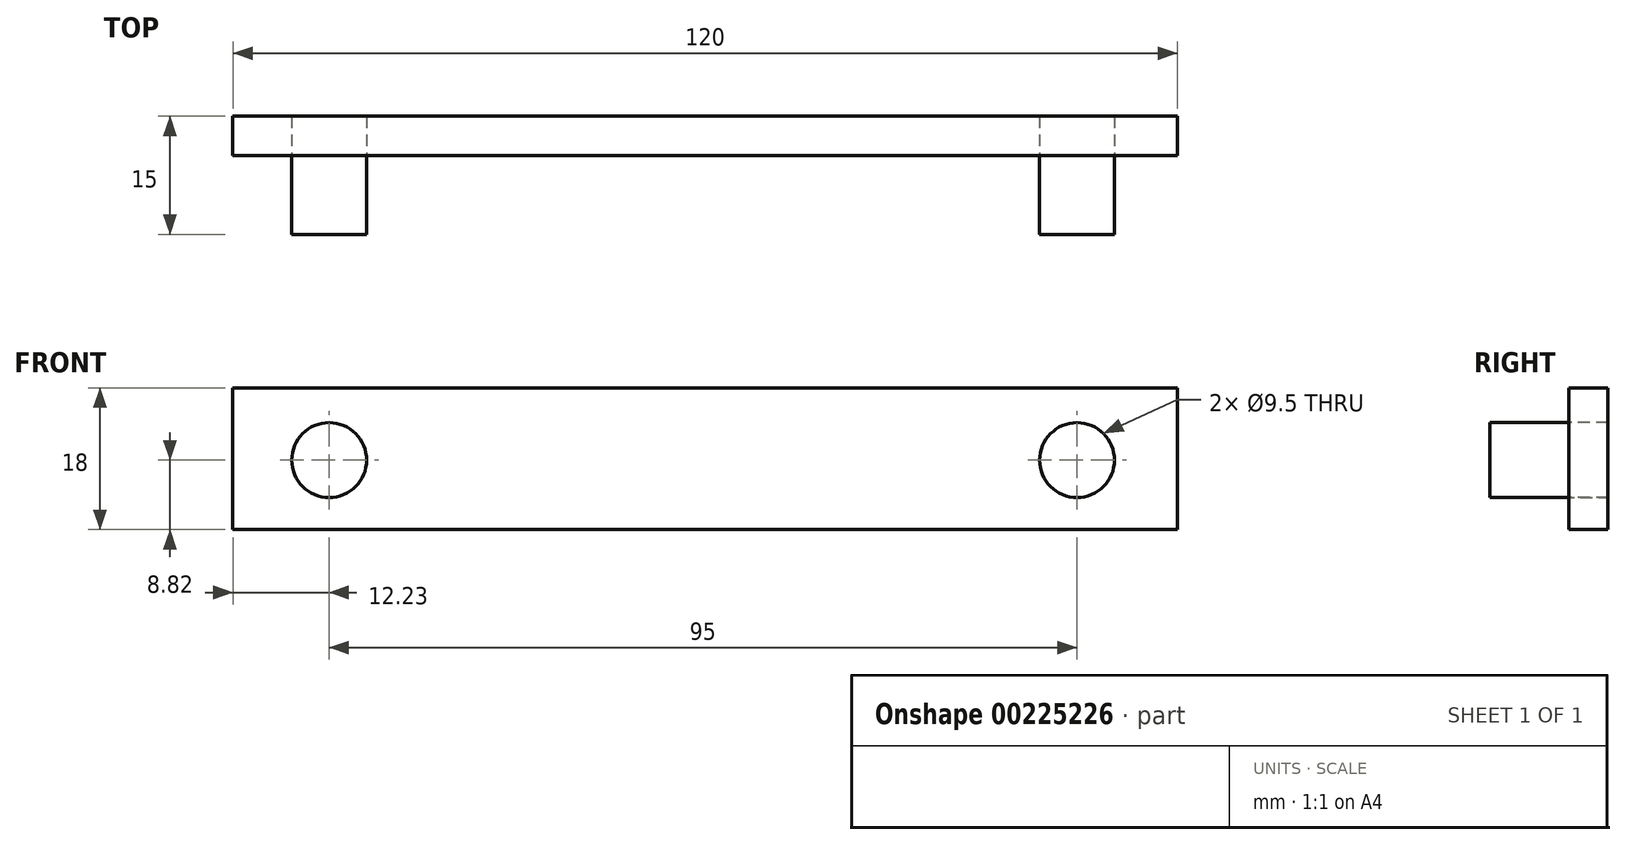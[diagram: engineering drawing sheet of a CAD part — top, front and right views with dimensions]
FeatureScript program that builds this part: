
annotation { "Feature Type Name" : "Feature", "Feature Type Description" : "" }
export const myFeature = defineFeature(function(context is Context, id is Id, definition is map)
    precondition{}
    {
        {
            var Q0;
            Q0=qCreatedBy(makeId("Front.planeOp"),FACE);
            var sketch = newSketch(context, id + "F0", { "sketchPlane" : qUnion([Q0])});
            skCircle(sketch, "E0", {"center": v(0, 0) * mm, "radius": 4.75 * mm});
            skLineSegment(sketch, "E1.bottom", {"start": v(-12.23, 9.18) * mm, "end": v(107.77, 9.18) * mm});
            skLineSegment(sketch, "E1.top", {"start": v(-12.23, -8.82) * mm, "end": v(107.77, -8.82) * mm});
            skLineSegment(sketch, "E1.left", {"start": v(-12.23, 9.18) * mm, "end": v(-12.23, -8.82) * mm});
            skLineSegment(sketch, "E1.right", {"start": v(107.77, 9.18) * mm, "end": v(107.77, -8.82) * mm});
            skCircle(sketch, "E2", {"center": v(95, 0) * mm, "radius": 4.75 * mm});
            skSolve(sketch);
        }
        {
            var Q0;
            Q0=makeQuery(id+"F0.imprint","IMPRINT",FACE,{"disambiguationData":[TD([[makeQuery(id+"F0.imprint","IMPRINT",EDGE,{"derivedFrom":sQuery(id+"F0.wireOp",EDGE,"E0")}),1.0]])]});
            var Q1;
            Q1=makeQuery(id+"F0.imprint","IMPRINT",FACE,{"disambiguationData":[TD([[makeQuery(id+"F0.imprint","IMPRINT",EDGE,{"derivedFrom":sQuery(id+"F0.wireOp",EDGE,"E2")}),1.0]])]});
            extrude(context, id + "F1", {"entities" : qUnion([Q0, Q1]), "depth" : 10 * mm, "hasSecondDirection" : true, "secondDirectionOppositeDirection" : true, "secondDirectionDepth" : 5 * mm, "offsetDistance" : 25 * mm});
        }
        {
            var Q0;
            Q0 = qSketchRegion(id + "F0", true);
            extrude(context, id + "F2", {"entities" : qUnion([Q0]), "oppositeDirection" : true, "depth" : 5 * mm, "offsetDistance" : 25 * mm});
        }
    });
